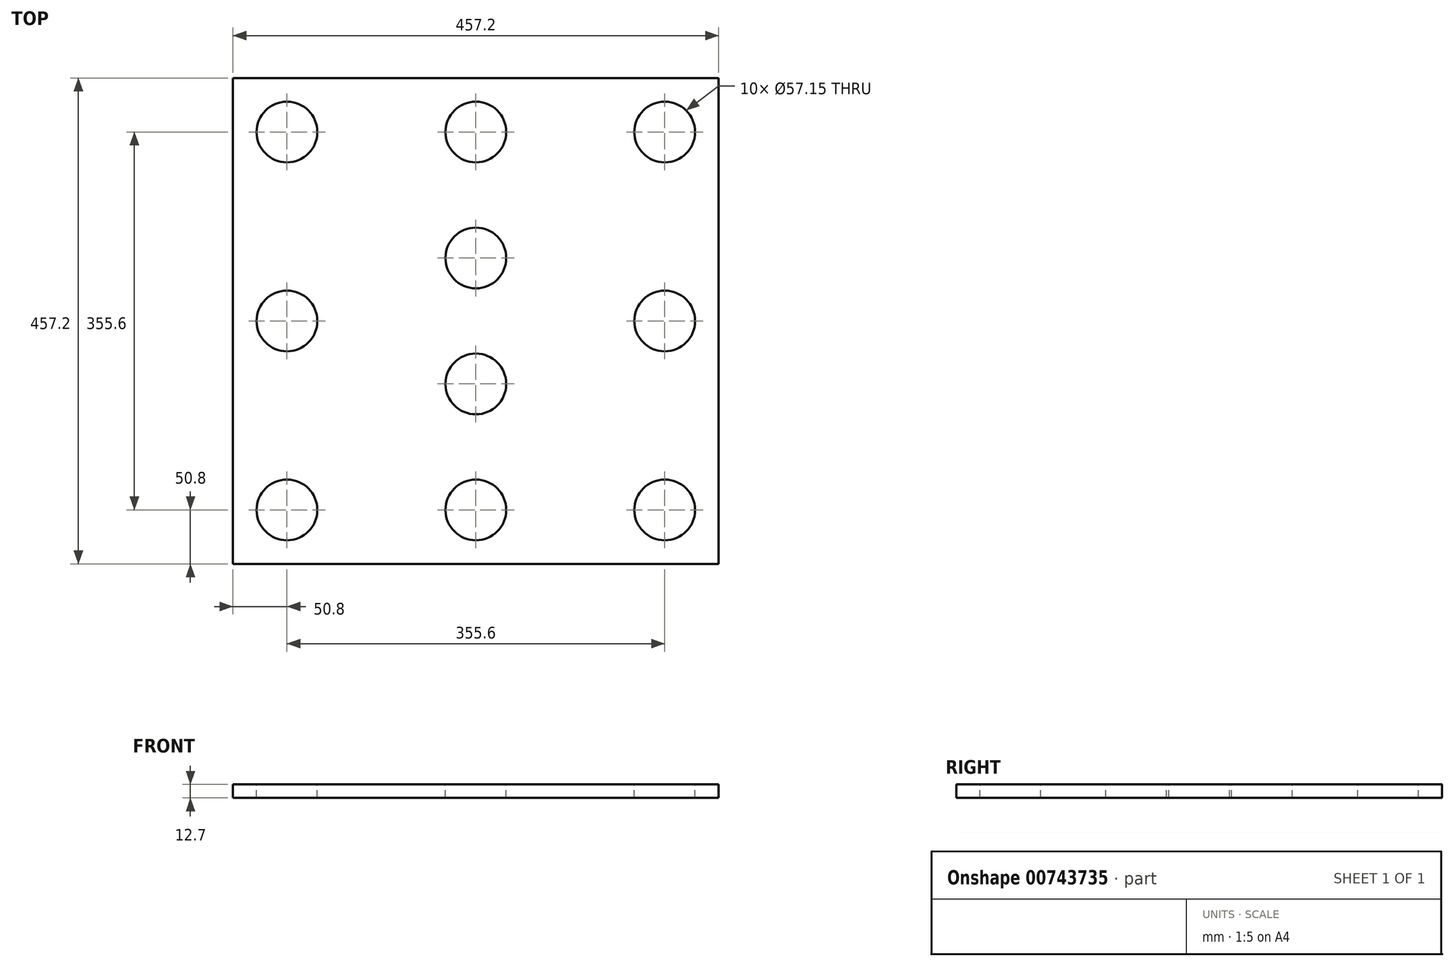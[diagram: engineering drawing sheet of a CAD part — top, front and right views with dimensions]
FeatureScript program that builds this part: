
annotation { "Feature Type Name" : "Feature", "Feature Type Description" : "" }
export const myFeature = defineFeature(function(context is Context, id is Id, definition is map)
    precondition{}
    {
        {
            var Q0;
            Q0=qCreatedBy(makeId("Top.planeOp"),FACE);
            var sketch = newSketch(context, id + "F0", { "sketchPlane" : qUnion([Q0])});
            skLineSegment(sketch, "E0.bottom", {"start": v(228.6, 228.6) * mm, "end": v(-228.6, 228.6) * mm});
            skLineSegment(sketch, "E0.top", {"start": v(228.6, -228.6) * mm, "end": v(-228.6, -228.6) * mm});
            skLineSegment(sketch, "E0.left", {"start": v(228.6, 228.6) * mm, "end": v(228.6, -228.6) * mm});
            skLineSegment(sketch, "E0.right", {"start": v(-228.6, 228.6) * mm, "end": v(-228.6, -228.6) * mm});
            skPoint(sketch, "E0.middle", {"position": v(0, 0) * mm});
            skSolve(sketch);
        }
        {
            var Q0;
            Q0=makeQuery(id+"F0.imprint","IMPRINT",FACE,{"disambiguationData":[TD([[makeQuery(id+"F0.imprint","IMPRINT",EDGE,{"derivedFrom":sQuery(id+"F0.wireOp",EDGE,"E0.bottom")}),1.0]])]});
            var sketch = newSketch(context, id + "F1", { "sketchPlane" : qUnion([Q0])});
            skCircle(sketch, "E1", {"center": v(-177.8, 177.8) * mm, "radius": 28.57 * mm});
            skCircle(sketch, "E2.1.0.0", {"center": v(0, 177.8) * mm, "radius": 28.57 * mm});
            skCircle(sketch, "E2.2.0.0", {"center": v(177.8, 177.8) * mm, "radius": 28.57 * mm});
            skLineSegment(sketch, "E2.direction1", {"start": v(-177.8, 177.8) * mm, "end": v(0, 177.8) * mm, "construction": true});
            skCircle(sketch, "E3.0.1.0", {"center": v(177.8, 0) * mm, "radius": 28.57 * mm});
            skCircle(sketch, "E3.0.2.0", {"center": v(177.8, -177.8) * mm, "radius": 28.57 * mm});
            skLineSegment(sketch, "E3.direction1", {"start": v(177.8, 177.8) * mm, "end": v(177.8, 177.8) * mm});
            skLineSegment(sketch, "E3.direction2", {"start": v(177.8, 177.8) * mm, "end": v(177.8, 0) * mm, "construction": true});
            skCircle(sketch, "E4.0.1.0", {"center": v(-177.8, 0) * mm, "radius": 28.57 * mm});
            skCircle(sketch, "E4.0.2.0", {"center": v(-177.8, -177.8) * mm, "radius": 28.57 * mm});
            skLineSegment(sketch, "E4.direction1", {"start": v(-177.8, 177.8) * mm, "end": v(-152.4, 177.8) * mm, "construction": true});
            skLineSegment(sketch, "E4.direction2", {"start": v(-177.8, 177.8) * mm, "end": v(-177.8, 0) * mm, "construction": true});
            skCircle(sketch, "E5.0.1.0", {"center": v(0, 59.27) * mm, "radius": 28.57 * mm});
            skCircle(sketch, "E5.0.2.0", {"center": v(0, -59.27) * mm, "radius": 28.57 * mm});
            skCircle(sketch, "E5.0.3.0", {"center": v(0, -177.8) * mm, "radius": 28.57 * mm});
            skLineSegment(sketch, "E5.direction1", {"start": v(0, 177.8) * mm, "end": v(363.22, 177.8) * mm, "construction": true});
            skLineSegment(sketch, "E5.direction2", {"start": v(0, 177.8) * mm, "end": v(0, 59.27) * mm, "construction": true});
            skSolve(sketch);
        }
        {
            var Q0;
            Q0 = qSketchRegion(id + "F0", true);
            extrude(context, id + "F2", {"entities" : qUnion([Q0]), "endBound" : BoundingType.SYMMETRIC, "depth" : 12.7 * mm, "offsetDistance" : 25.4 * mm});
        }
        {
            var Q0;
            Q0 = qSketchRegion(id + "F1", true);
            extrude(context, id + "F3", {"entities" : qUnion([Q0]), "operationType" : NewBodyOperationType.REMOVE, "endBound" : BoundingType.SYMMETRIC, "oppositeDirection" : true, "depth" : 25.4 * mm, "offsetDistance" : 25.4 * mm});
        }
    });
